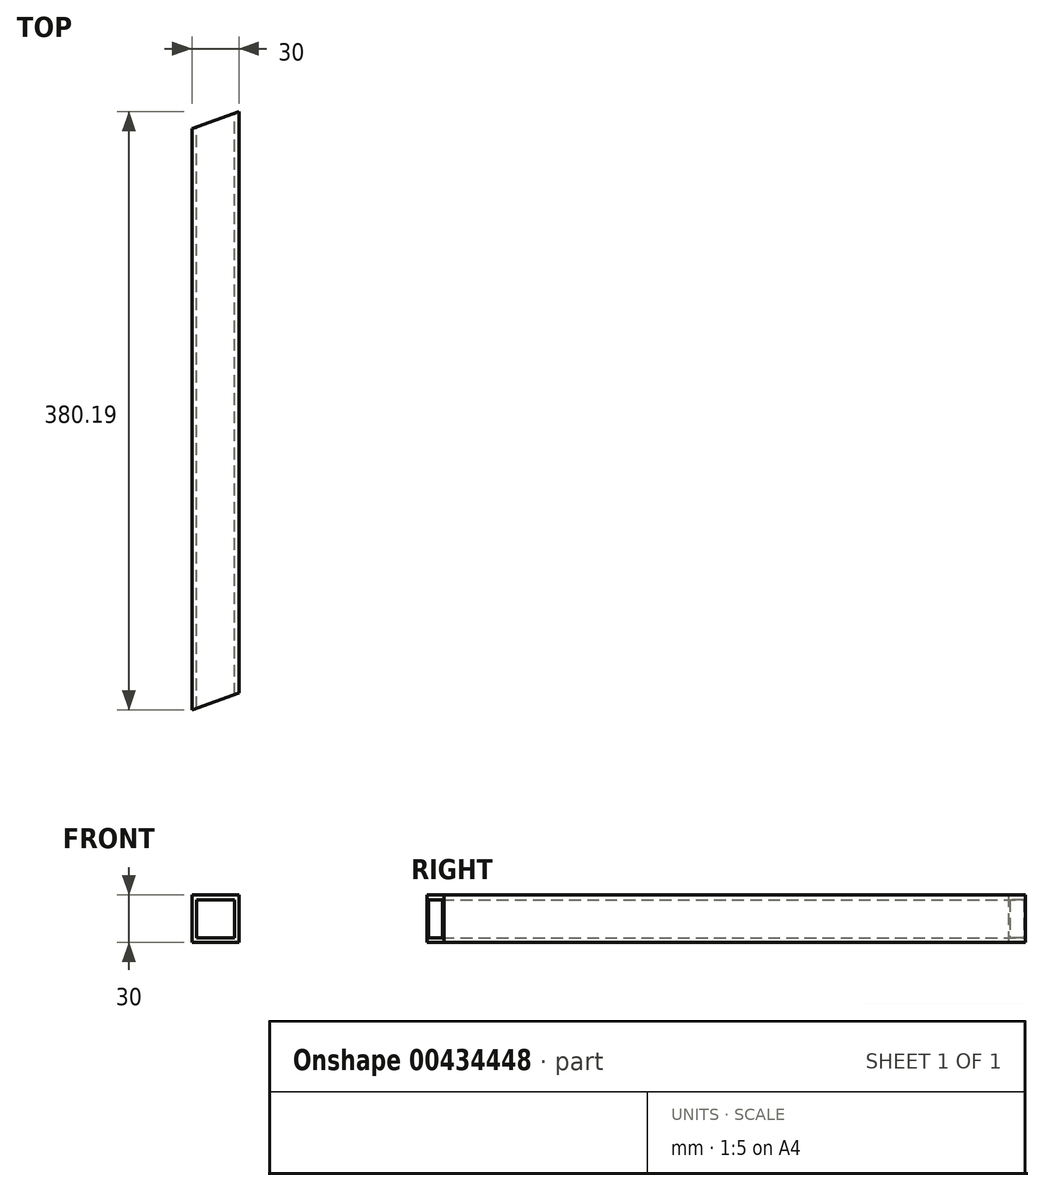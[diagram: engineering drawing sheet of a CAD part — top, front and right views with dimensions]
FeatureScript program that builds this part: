
annotation { "Feature Type Name" : "Feature", "Feature Type Description" : "" }
export const myFeature = defineFeature(function(context is Context, id is Id, definition is map)
    precondition{}
    {
        {
            var Q0;
            Q0=qCreatedBy(makeId("Front.planeOp"),FACE);
            var sketch = newSketch(context, id + "F0", { "sketchPlane" : qUnion([Q0])});
            skLineSegment(sketch, "E0.bottom", {"start": v(15, 15) * mm, "end": v(-15, 15) * mm});
            skLineSegment(sketch, "E0.top", {"start": v(15, -15) * mm, "end": v(-15, -15) * mm});
            skLineSegment(sketch, "E0.left", {"start": v(15, 15) * mm, "end": v(15, -15) * mm});
            skLineSegment(sketch, "E0.right", {"start": v(-15, 15) * mm, "end": v(-15, -15) * mm});
            skPoint(sketch, "E0.middle", {"position": v(0, 0) * mm});
            skLineSegment(sketch, "E1.bottom", {"start": v(12, 12) * mm, "end": v(-12, 12) * mm});
            skLineSegment(sketch, "E1.top", {"start": v(12, -12) * mm, "end": v(-12, -12) * mm});
            skLineSegment(sketch, "E1.left", {"start": v(12, 12) * mm, "end": v(12, -12) * mm});
            skLineSegment(sketch, "E1.right", {"start": v(-12, 12) * mm, "end": v(-12, -12) * mm});
            skSolve(sketch);
        }
        {
            var Q0;
            Q0 = qSketchRegion(id + "F0", true);
            extrude(context, id + "F1", {"entities" : qUnion([Q0]), "depth" : 500 * mm, "offsetDistance" : 25 * mm});
        }
        {
            var Q0;
            Q0=makeQuery(id+"F1.opExtrude","SWEPT_FACE",FACE,{"disambiguationData":[OSD([sQuery(id+"F0.wireOp",EDGE,"E0.top")])]});
            var sketch = newSketch(context, id + "F2", { "sketchPlane" : qUnion([Q0])});
            skLineSegment(sketch, "E2", {"start": v(15, 369.27) * mm, "end": v(15, 500) * mm});
            skLineSegment(sketch, "E3", {"start": v(15, 500) * mm, "end": v(-15, 500) * mm});
            skLineSegment(sketch, "E4", {"start": v(15, 0) * mm, "end": v(-15, 10.92) * mm});
            skLineSegment(sketch, "E5", {"start": v(-15, 10.92) * mm, "end": v(-15, 0) * mm});
            skLineSegment(sketch, "E6", {"start": v(-15, 0) * mm, "end": v(15, 0) * mm});
            skLineSegment(sketch, "E7", {"start": v(15, 369.27) * mm, "end": v(-15, 380.19) * mm});
            skLineSegment(sketch, "E8", {"start": v(-15, 380.19) * mm, "end": v(-15, 500) * mm});
            skSolve(sketch);
        }
        {
            var Q0;
            Q0 = qSketchRegion(id + "F2", true);
            extrude(context, id + "F3", {"entities" : qUnion([Q0]), "operationType" : NewBodyOperationType.REMOVE, "endBound" : BoundingType.THROUGH_ALL, "oppositeDirection" : true, "depth" : 25 * mm, "offsetDistance" : 25 * mm});
        }
    });
